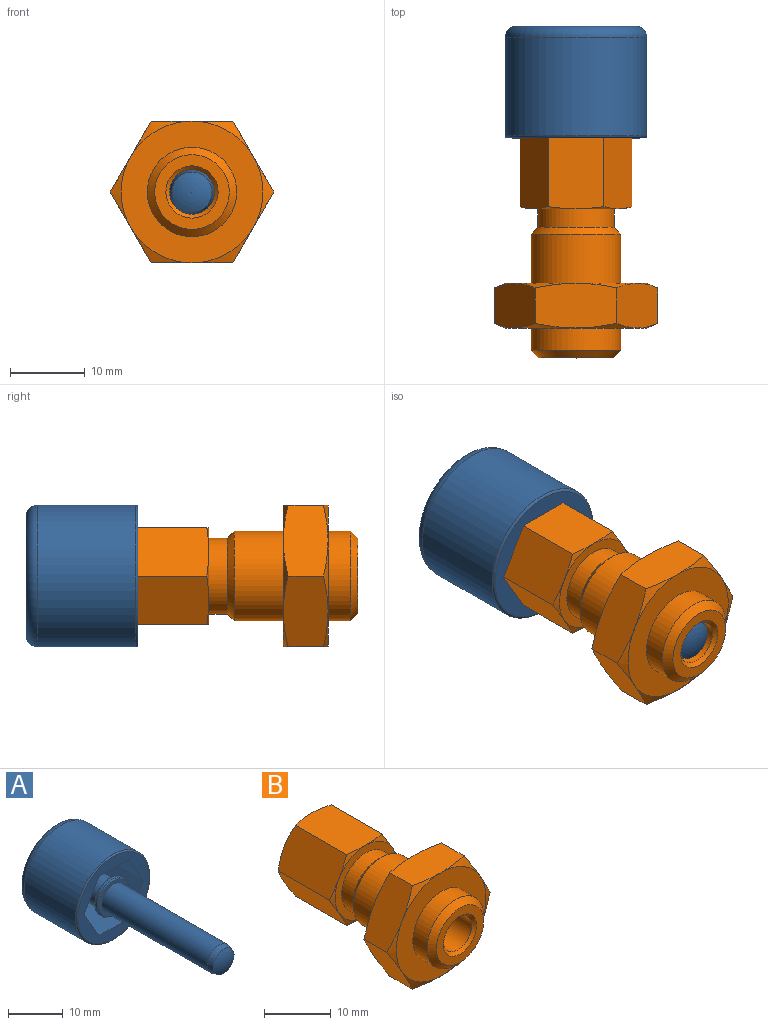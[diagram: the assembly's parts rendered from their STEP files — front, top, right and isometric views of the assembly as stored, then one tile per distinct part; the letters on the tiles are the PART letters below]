
ASSEMBLY  parts=2 mates=1
PART A: 22 faces, bbox 20.6x44x20.6 mm
  f0: plane 15.24x13.2mm, normal (0,-1,0), area 122.6mm2, adj f1,f10,f11,f12,f13,f14,f15
  f1: cylinder r=3mm len=11mm, axis (0,-1,0), area 207.3mm2, adj f0,f2
  f2: plane 7.6x7.6mm, normal (0,1,0), area 17.1mm2, adj f1,f3
  f3: torus R=3.8mm, axis (0,-1,0), area 7.8mm2, adj f2,f4
  f4: cylinder r=4mm len=8mm, axis (0,-1,0), area 15.1mm2, adj f3,f5
  f5: torus R=3.8mm, axis (0,-1,0), area 7.8mm2, adj f4,f6
  f6: plane 7.6x7.6mm, normal (0,-1,0), area 17.1mm2, adj f5,f7
  f7: cylinder r=3mm len=27.2mm, axis (0,-1,0), area 512.6mm2, adj f6,f8
  f8: cone r=3mm half-angle=15deg, axis (0,1,0), area 21.6mm2, adj f7,f9
  f9: torus R=0mm, axis (0,-1,0), area 23.9mm2, adj f8
  f10: plane 12x6.6mm, normal (0.87,0,-0.5), area 91.5mm2, adj f0,f11,f15,f21
  f11: plane 12x6.6mm, normal (0.87,0,0.5), area 91.5mm2, adj f0,f10,f12,f21
  f12: plane 12x7.62mm, normal (0,0,1), area 91.5mm2, adj f0,f11,f13,f21
  f13: plane 12x6.6mm, normal (-0.87,0,0.5), area 91.5mm2, adj f0,f12,f14,f21
  f14: plane 12x6.6mm, normal (-0.87,0,-0.5), area 91.5mm2, adj f0,f13,f15,f21
  f15: plane 12x7.62mm, normal (0,0,-1), area 91.5mm2, adj f0,f10,f14,f21
  f16: torus R=0mm, axis (0,-1,0), area 155.7mm2, adj f17
  f17: plane 16x16mm, normal (0,1,0), area 45.9mm2, adj f16,f18
  f18: torus R=8mm, axis (0,-1,0), area 132.6mm2, adj f17,f19
  f19: cylinder r=9.5mm len=19mm, axis (0,-1,0), area 787.9mm2, adj f18,f20
  f20: torus R=9.2mm, axis (0,-1,0), area 27.8mm2, adj f19,f21
  f21: plane 18.4x18.4mm, normal (0,-1,0), area 115mm2, adj f10,f11,f12,f13,f14,f15,f20
PART B: 61 faces, bbox 22.8x32.8x22.8 mm
  f0: cone r=6.5mm half-angle=75deg, axis (0,1,0), area 3.7mm2, adj f33,f56,f57
  f1: cone r=6.5mm half-angle=75deg, axis (0,1,0), area 3.7mm2, adj f33,f57,f58
  f2: cone r=6.5mm half-angle=75deg, axis (0,1,0), area 3.7mm2, adj f33,f55,f56
  f3: cone r=6.5mm half-angle=75deg, axis (0,1,0), area 3.7mm2, adj f33,f58,f59
  f4: cone r=6.5mm half-angle=75deg, axis (0,1,0), area 3.7mm2, adj f33,f55,f60
  f5: cone r=9.5mm half-angle=67.5deg, axis (0,-1,0), area 8.3mm2, adj f15,f20,f21
  f6: cone r=9.5mm half-angle=67.5deg, axis (0,-1,0), area 8.3mm2, adj f15,f21,f22
  f7: cone r=9.5mm half-angle=67.5deg, axis (0,-1,0), area 8.3mm2, adj f15,f19,f20
  f8: cone r=9.5mm half-angle=67.5deg, axis (0,-1,0), area 8.3mm2, adj f15,f22,f23
  f9: cone r=9.5mm half-angle=67.5deg, axis (0,-1,0), area 8.3mm2, adj f15,f19,f24
  f10: cone r=11.4mm half-angle=67.5deg, axis (0,1,0), area 8.3mm2, adj f18,f19,f24
  f11: cone r=11.4mm half-angle=67.5deg, axis (0,1,0), area 8.3mm2, adj f18,f19,f20
  f12: cone r=11.4mm half-angle=67.5deg, axis (0,1,0), area 8.3mm2, adj f18,f20,f21
  f13: cone r=11.4mm half-angle=67.5deg, axis (0,1,0), area 8.3mm2, adj f18,f21,f22
  f14: cone r=11.4mm half-angle=67.5deg, axis (0,1,0), area 8.3mm2, adj f18,f22,f23
  f15: plane 19x19mm, normal (0,1,0), area 170.4mm2, adj f5,f6,f7,f8,f9,f16,f25
  f16: cone r=9.5mm half-angle=67.5deg, axis (0,-1,0), area 8.3mm2, adj f15,f23,f24
  f17: cone r=11.4mm half-angle=67.5deg, axis (0,1,0), area 8.3mm2, adj f18,f23,f24
  f18: plane 19x19mm, normal (0,-1,0), area 170.4mm2, adj f10,f11,f12,f13,f14,f17,f30
  f19: plane 10.35x6.85mm, normal (-0.87,0,-0.5), area 61.2mm2, adj f7,f9,f10,f11,f20,f24
  f20: plane 11.82x6.85mm, normal (0,0,-1), area 61.2mm2, adj f5,f7,f11,f12,f19,f21
  f21: plane 10.35x6.85mm, normal (0.87,0,-0.5), area 61.2mm2, adj f5,f6,f12,f13,f20,f22
  f22: plane 10.35x6.85mm, normal (0.87,0,0.5), area 61.2mm2, adj f6,f8,f13,f14,f21,f23
  f23: plane 11.82x6.85mm, normal (0,0,1), area 61.2mm2, adj f8,f14,f16,f17,f22,f24
  f24: plane 10.35x6.85mm, normal (-0.87,0,0.5), area 61.2mm2, adj f9,f10,f16,f17,f19,f23
  f25: cylinder r=6mm len=12mm, axis (0,-1,0), area 248.8mm2, adj f15,f31
  f26: cylinder r=3mm len=19.5mm, axis (0,-1,0), area 367.6mm2, adj f27,f54
  f27: cone r=3mm half-angle=45deg, axis (0,-1,0), area 14.4mm2, adj f26,f28
  f28: plane 10x10mm, normal (0,-1,0), area 40.1mm2, adj f27,f29
  f29: cone r=5mm half-angle=45deg, axis (0,1,0), area 48.9mm2, adj f28,f30
  f30: cylinder r=6mm len=12mm, axis (0,-1,0), area 113.1mm2, adj f18,f29
  f31: cone r=6mm half-angle=45deg, axis (0,-1,0), area 44.4mm2, adj f25,f32
  f32: cylinder r=5.1mm len=10.2mm, axis (0,-1,0), area 80.1mm2, adj f31,f33
  f33: plane 13x13mm, normal (0,-1,0), area 51mm2, adj f0,f1,f2,f3,f4,f32,f34
  f34: cone r=6.5mm half-angle=75deg, axis (0,1,0), area 3.7mm2, adj f33,f59,f60
  f35: cone r=8.33mm half-angle=60deg, axis (0,-1,0), area 43.3mm2, adj f36,f55,f56,f57,f58,f59,f60
  f36: plane 11.84x11.84mm, normal (0,1,0), area 81.9mm2, adj f35,f37
  f37: cylinder r=3mm len=6mm, axis (0,-1,0), area 28.3mm2, adj f36,f38
  f38: plane 7.6x7.6mm, normal (0,-1,0), area 17.1mm2, adj f37,f39
  f39: torus R=3.8mm, axis (0,-1,0), area 7.8mm2, adj f38,f40
  f40: cylinder r=4mm len=8mm, axis (0,-1,0), area 15.1mm2, adj f39,f41
  f41: torus R=3.8mm, axis (0,-1,0), area 7.8mm2, adj f40,f42
  f42: plane 7.6x7.6mm, normal (0,1,0), area 17.1mm2, adj f41,f43
  f43: cylinder r=3mm len=6mm, axis (0,-1,0), area 103.7mm2, adj f42,f44
  f44: plane 7.6x7.6mm, normal (0,-1,0), area 17.1mm2, adj f43,f45
  f45: torus R=3.8mm, axis (0,-1,0), area 7.8mm2, adj f44,f46
  f46: cylinder r=4mm len=8mm, axis (0,-1,0), area 15.1mm2, adj f45,f47
  f47: torus R=3.8mm, axis (0,-1,0), area 7.8mm2, adj f46,f48
  f48: plane 7.6x7.6mm, normal (0,1,0), area 17.1mm2, adj f47,f49
  f49: cylinder r=3mm len=6mm, axis (0,-1,0), area 37.7mm2, adj f48,f50
  f50: plane 7.6x7.6mm, normal (0,-1,0), area 17.1mm2, adj f49,f51
  f51: torus R=3.8mm, axis (0,-1,0), area 7.8mm2, adj f50,f52
  f52: cylinder r=4mm len=8mm, axis (0,-1,0), area 15.1mm2, adj f51,f53
  f53: torus R=3.8mm, axis (0,-1,0), area 7.8mm2, adj f52,f54
  f54: plane 7.6x7.6mm, normal (0,1,0), area 17.1mm2, adj f26,f53
  f55: plane 12.23x7.06mm, normal (-0.87,0,-0.5), area 85.4mm2, adj f2,f4,f35,f56,f60
  f56: plane 12.29x8.13mm, normal (0,0,-1), area 85.4mm2, adj f0,f2,f35,f55,f57
  f57: plane 12.23x7.06mm, normal (0.87,0,-0.5), area 85.4mm2, adj f0,f1,f35,f56,f58
  f58: plane 12.23x7.06mm, normal (0.87,0,0.5), area 85.4mm2, adj f1,f3,f35,f57,f59
  f59: plane 12.23x8.07mm, normal (0,0,1), area 85.4mm2, adj f3,f34,f35,f58,f60
  f60: plane 12.23x7.06mm, normal (-0.87,0,0.5), area 85.4mm2, adj f4,f34,f35,f55,f59
PLACE A t=(0,6.5,0)mm
PLACE B at identity fixed
MATE fastened A.f1 <-> B.f0  axis (0,-1,0) through (0,29.5,0)mm
